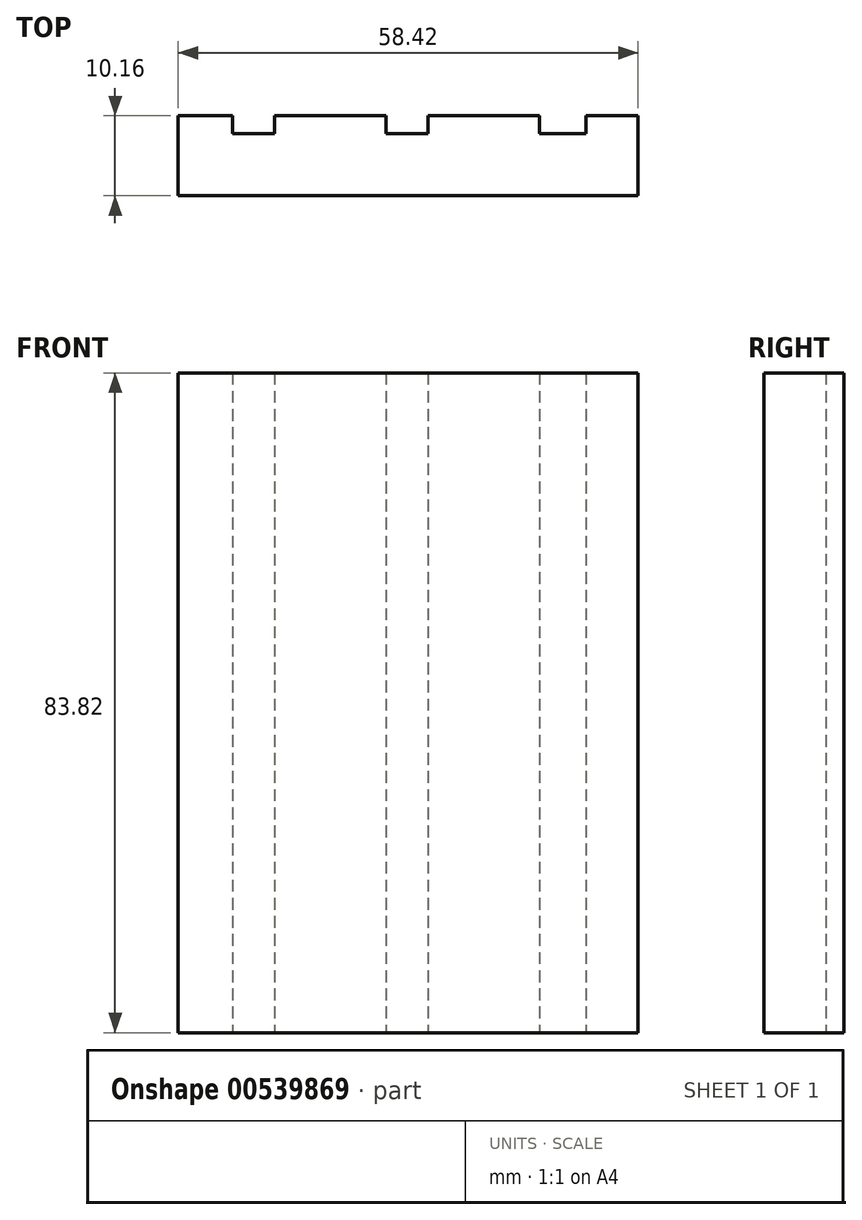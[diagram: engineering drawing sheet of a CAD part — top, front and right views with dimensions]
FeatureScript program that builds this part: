
annotation { "Feature Type Name" : "Feature", "Feature Type Description" : "" }
export const myFeature = defineFeature(function(context is Context, id is Id, definition is map)
    precondition{}
    {
        {
            var Q0;
            Q0=qCreatedBy(makeId("Front.planeOp"),FACE);
            var sketch = newSketch(context, id + "F0", { "sketchPlane" : qUnion([Q0])});
            skLineSegment(sketch, "E0.bottom", {"start": v(0, 0) * mm, "end": v(58.42, 0) * mm});
            skLineSegment(sketch, "E0.top", {"start": v(0, 83.82) * mm, "end": v(58.42, 83.82) * mm});
            skLineSegment(sketch, "E0.left", {"start": v(0, 0) * mm, "end": v(0, 83.82) * mm});
            skLineSegment(sketch, "E0.right", {"start": v(58.42, 0) * mm, "end": v(58.42, 83.82) * mm});
            skSolve(sketch);
        }
        {
            var Q0;
            Q0 = qSketchRegion(id + "F0", true);
            extrude(context, id + "F1", {"entities" : qUnion([Q0]), "depth" : 10.16 * mm, "offsetDistance" : 25.4 * mm});
        }
        {
            var Q0;
            Q0=qCreatedBy(makeId("Front.planeOp"),FACE);
            var sketch = newSketch(context, id + "F2", { "sketchPlane" : qUnion([Q0])});
            skLineSegment(sketch, "E1", {"start": v(6.89, 83.82) * mm, "end": v(6.89, 0) * mm});
            skLineSegment(sketch, "E2", {"start": v(12.22, 83.82) * mm, "end": v(12.22, 0) * mm});
            skLineSegment(sketch, "E3", {"start": v(26.4, 83.82) * mm, "end": v(26.4, 0) * mm});
            skLineSegment(sketch, "E4", {"start": v(31.72, 83.82) * mm, "end": v(31.72, 0) * mm});
            skLineSegment(sketch, "E5", {"start": v(51.77, 83.82) * mm, "end": v(51.77, 0) * mm});
            skLineSegment(sketch, "E6", {"start": v(45.9, 83.82) * mm, "end": v(45.9, 0) * mm});
            skLineSegment(sketch, "E7", {"start": v(6.89, 83.82) * mm, "end": v(12.22, 83.82) * mm});
            skLineSegment(sketch, "E8", {"start": v(12.22, 0) * mm, "end": v(6.89, 0) * mm});
            skLineSegment(sketch, "E9", {"start": v(26.4, 0) * mm, "end": v(31.72, 0) * mm});
            skLineSegment(sketch, "E10", {"start": v(31.72, 83.82) * mm, "end": v(26.4, 83.82) * mm});
            skLineSegment(sketch, "E11", {"start": v(45.9, 83.82) * mm, "end": v(51.77, 83.82) * mm});
            skLineSegment(sketch, "E12", {"start": v(51.77, 0) * mm, "end": v(45.9, 0) * mm});
            skSolve(sketch);
        }
        {
            var Q0;
            Q0 = qSketchRegion(id + "F2", true);
            extrude(context, id + "F3", {"entities" : qUnion([Q0]), "operationType" : NewBodyOperationType.REMOVE, "depth" : 2.3 * mm, "offsetDistance" : 25.4 * mm});
        }
    });
